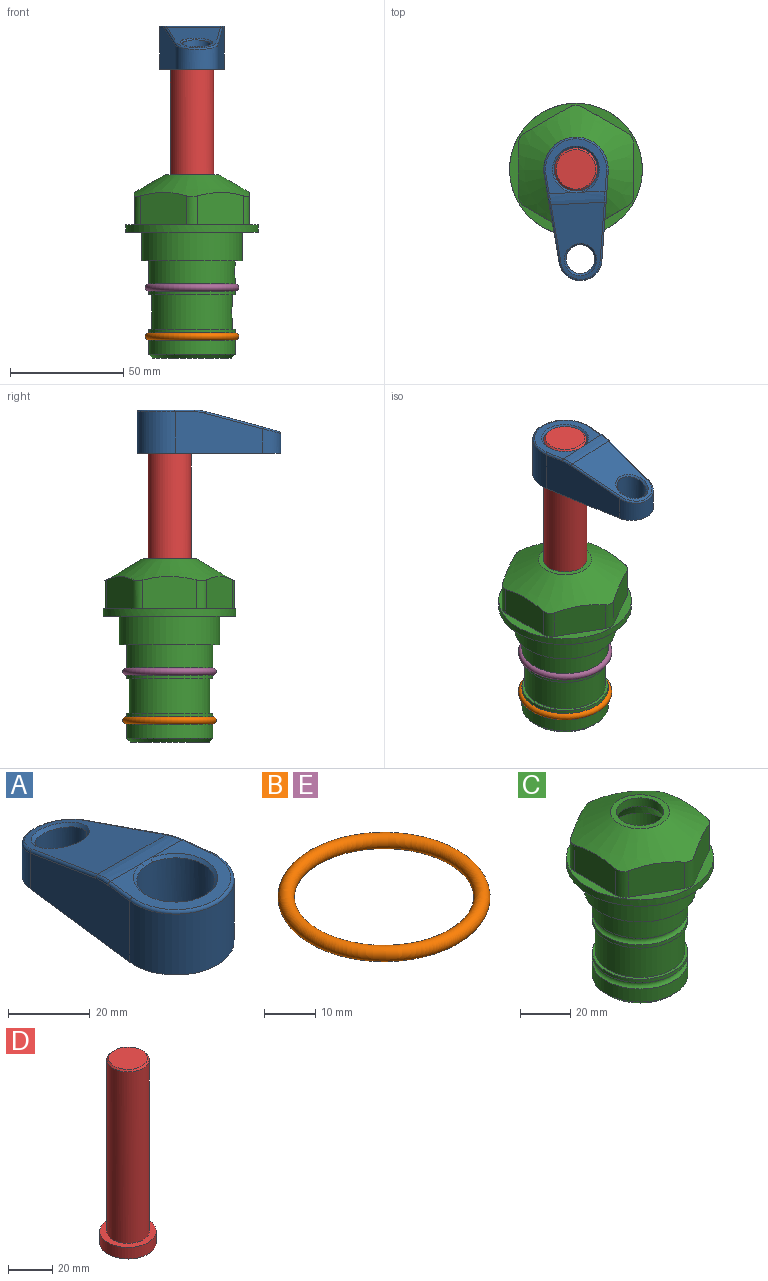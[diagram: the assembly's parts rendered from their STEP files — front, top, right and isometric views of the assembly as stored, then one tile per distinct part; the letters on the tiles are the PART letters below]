
ASSEMBLY  parts=5 mates=4
PART A: 31 faces, bbox 31.7x65.5x19.8 mm
  f0: plane 39.12x18.26mm, normal (0.99,0.12,0), area 612.2mm2, adj f1,f4,f7,f11,f13,f15
  f1: cylinder r=9.53mm len=18.91mm, axis (0,0,-1), area 296.1mm2, adj f0,f2,f7,f17
  f2: plane 39.12x18.26mm, normal (-0.99,0.12,0), area 612.2mm2, adj f1,f4,f7,f12,f14,f16
  f3: cylinder r=6.35mm len=12.7mm, axis (0,0,-1), area 362.4mm2, adj f7,f18
  f4: cylinder r=14.29mm len=28.58mm, axis (0,0,-1), area 882.2mm2, adj f0,f2,f7,f10
  f5: cylinder r=9.53mm len=19.05mm, axis (0,0,-1), area 1092.6mm2, adj f7,f19,f20
  f6: plane 26.99x23.69mm, normal (0,0,1), area 216.2mm2, adj f9,f10,f11,f12,f19
  f7: plane 63.5x28.58mm, normal (0,0,-1), area 661.8mm2, adj f0,f1,f2,f3,f4,f5,f22,f23
  f8: plane 33.52x23.6mm, normal (0,0.26,0.97), area 486mm2, adj f9,f15,f16,f17,f18
  f9: cylinder r=19.05mm len=24.72mm, axis (1,0,0), area 120.4mm2, adj f6,f8,f13,f14,f20
  f10: torus R=13.49mm, axis (0,0,1), area 59mm2, adj f4,f6,f11,f12
  f11: cylinder r=0.79mm len=8.67mm, axis (0.12,-0.99,0), area 10.8mm2, adj f0,f6,f10,f13
  f12: cylinder r=0.79mm len=8.67mm, axis (0.12,0.99,0), area 10.8mm2, adj f2,f6,f10,f14
  f13: bspline ~4.95x1.42mm, area 6.1mm2, adj f0,f9,f11,f15
  f14: bspline ~4.95x1.42mm, area 6.1mm2, adj f2,f9,f12,f16
  f15: cylinder r=0.79mm len=25.95mm, axis (0.12,-0.96,0.26), area 32.9mm2, adj f0,f8,f13,f17
  f16: cylinder r=0.79mm len=25.95mm, axis (0.12,0.96,-0.26), area 32.9mm2, adj f2,f8,f14,f17
  f17: bspline ~18.91x8.38mm, area 30mm2, adj f1,f8,f15,f16
  f18: bspline ~14.29x14.29mm, area 48.3mm2, adj f3,f8
  f19: cone r=9.53mm half-angle=45deg, axis (0,0,1), area 66.5mm2, adj f5,f6,f20
  f20: bspline ~3.22x0.96mm, area 3.5mm2, adj f5,f9,f19
  f21: plane 2.75x2.72mm, normal (0,0,-1), area 2.9mm2, adj f23,f25,f28
  f22: plane 23.05x15.88mm, normal (-0.99,-0.12,0), area 323.6mm2, adj f7,f25,f26,f27,f28,f29
  f23: plane 23.05x15.88mm, normal (0.99,-0.12,0), area 323.6mm2, adj f7,f21,f25,f27,f28,f30
  f24: cylinder r=9.53mm len=10.69mm, axis (0,0,-1), area 114.7mm2, adj f7,f27,f29,f30
  f25: cylinder r=12.7mm len=20.59mm, axis (0,0,-1), area 381.1mm2, adj f7,f21,f22,f23,f26,f28
  f26: plane 2.75x2.72mm, normal (0,0,-1), area 2.9mm2, adj f22,f25,f28
  f27: plane 19.72x18.37mm, normal (0,-0.26,-0.97), area 291.8mm2, adj f22,f23,f24,f28,f29,f30
  f28: cylinder r=15.88mm len=19.92mm, axis (1,0,0), area 54.8mm2, adj f21,f22,f23,f25,f26,f27
  f29: cylinder r=1.59mm len=11mm, axis (0,0,-1), area 34.7mm2, adj f7,f22,f24,f27
  f30: cylinder r=1.59mm len=11mm, axis (0,0,-1), area 34.7mm2, adj f7,f23,f24,f27
PART B: 1 faces, bbox 44.7x44.7x3.2 mm
  f0: torus R=19.05mm, axis (0,0,1), area 1193.9mm2
PART C: 36 faces, bbox 58.7x58.7x81 mm
  f0: cylinder r=17.78mm len=35.56mm, axis (0,0,1), area 1670.8mm2, adj f23,f24,f31
  f1: cylinder r=19.05mm len=38.1mm, axis (0,0,1), area 1191.9mm2, adj f26,f27,f30
  f2: plane 58.66x58.66mm, normal (0,0,-1), area 1150.6mm2, adj f3,f28
  f3: cylinder r=29.33mm len=58.66mm, axis (0,0,-1), area 585.1mm2, adj f2,f4
  f4: plane 58.66x58.66mm, normal (0,0,1), area 475.9mm2, adj f3,f5,f6,f7,f8,f9,f10,f11
  f5: plane 20.32x14.34mm, normal (-0.5,0.87,0), area 324.4mm2, adj f4,f15,f16,f17
  f6: plane 20.32x14.34mm, normal (0.5,0.87,0), area 324.4mm2, adj f4,f14,f15,f17
  f7: plane 23.48x14.34mm, normal (1,0,0), area 324.4mm2, adj f4,f13,f14,f17
  f8: plane 20.32x14.34mm, normal (0.5,-0.87,0), area 324.4mm2, adj f4,f12,f13,f17
  f9: plane 20.32x14.34mm, normal (-0.5,-0.87,0), area 324.4mm2, adj f4,f11,f12,f17
  f10: plane 23.48x14.34mm, normal (-1,0,0), area 324.4mm2, adj f4,f11,f16,f17
  f11: cylinder r=5.08mm len=12.85mm, axis (0,0,-1), area 67.2mm2, adj f4,f9,f10,f17
  f12: cylinder r=5.08mm len=12.85mm, axis (0,0,-1), area 67.2mm2, adj f4,f8,f9,f17
  f13: cylinder r=5.08mm len=12.85mm, axis (0,0,-1), area 67.2mm2, adj f4,f7,f8,f17
  f14: cylinder r=5.08mm len=12.85mm, axis (0,0,-1), area 67.2mm2, adj f4,f6,f7,f17
  f15: cylinder r=5.08mm len=12.85mm, axis (0,0,-1), area 67.2mm2, adj f4,f5,f6,f17
  f16: cylinder r=5.08mm len=12.85mm, axis (0,0,-1), area 67.2mm2, adj f4,f5,f10,f17
  f17: cone r=11.73mm half-angle=60deg, axis (0,0,-1), area 2071.8mm2, adj f5,f6,f7,f8,f9,f10,f11,f12
  f18: plane 23.46x23.46mm, normal (0,0,1), area 147.4mm2, adj f17,f35
  f19: plane 34.93x34.93mm, normal (0,0,-1), area 958mm2, adj f29
  f20: cylinder r=19.05mm len=38.1mm, axis (0,0,1), area 760.1mm2, adj f21,f29
  f21: torus R=19.05mm, axis (0,0,1), area 565.3mm2, adj f20,f22
  f22: cylinder r=19.05mm len=38.1mm, axis (0,0,1), area 190mm2, adj f21,f23
  f23: plane 38.1x38.1mm, normal (0,0,1), area 146.9mm2, adj f0,f22
  f24: plane 38.1x38.1mm, normal (0,0,-1), area 146.9mm2, adj f0,f25
  f25: cylinder r=19.05mm len=38.1mm, axis (0,0,1), area 190mm2, adj f24,f26
  f26: torus R=19.05mm, axis (0,0,1), area 565.3mm2, adj f1,f25
  f27: plane 44.45x44.45mm, normal (0,0,-1), area 411.7mm2, adj f1,f28
  f28: cylinder r=22.23mm len=44.45mm, axis (0,0,1), area 1773.5mm2, adj f2,f27
  f29: cone r=19.05mm half-angle=45deg, axis (0,0,1), area 257.5mm2, adj f19,f20
  f30: cylinder r=3.17mm len=6.75mm, axis (-1,0,0), area 128mm2, adj f1,f33
  f31: cylinder r=3.17mm len=6.35mm, axis (-1,0,0), area 102.5mm2, adj f0,f33
  f32: plane 25.4x25.4mm, normal (0,0,1), area 506.7mm2, adj f33
  f33: cylinder r=12.7mm len=66.42mm, axis (0,0,-1), area 5236.2mm2, adj f30,f31,f32,f34
  f34: cone r=9.53mm half-angle=30deg, axis (0,0,-1), area 443.4mm2, adj f33,f35
  f35: cylinder r=9.53mm len=19.05mm, axis (0,0,-1), area 240.9mm2, adj f18,f34
PART D: 6 faces, bbox 25.4x25.4x101.6 mm
  f0: plane 17.46x17.46mm, normal (0,0,1), area 239.5mm2, adj f5
  f1: plane 25.4x25.4mm, normal (0,0,-1), area 506.7mm2, adj f2
  f2: cylinder r=12.7mm len=25.4mm, axis (0,0,1), area 506.7mm2, adj f1,f3
  f3: plane 25.4x25.4mm, normal (0,0,1), area 221.7mm2, adj f2,f4
  f4: cylinder r=9.53mm len=94.46mm, axis (0,0,1), area 5653mm2, adj f3,f5
  f5: cone r=8.73mm half-angle=45deg, axis (0,0,-1), area 64.4mm2, adj f0,f4
PART E: same geometry as B
PLACE A rot(axis=(0,0,-1),177.2deg) t=(0,0,27.55)mm
PLACE B t=(0,0,-21.59)mm
PLACE C at identity fixed
PLACE D rot(axis=(0,0,-1),177.2deg) t=(0,0,27.55)mm
PLACE E at identity
MATE fastened B.f0 <-> C.f0  axis (0,0,1) through (0,0,-46.1)mm
MATE fastened E.f0 <-> C.f0  axis (0,0,1) through (0,0,-24.51)mm
MATE cylindrical D.f2 <-> C.f0  axis (0,0,1) through (0,0,-10.55)mm
MATE fastened D.f2 <-> A.f4  axis (0,0,1) through (0,0,91.05)mm
